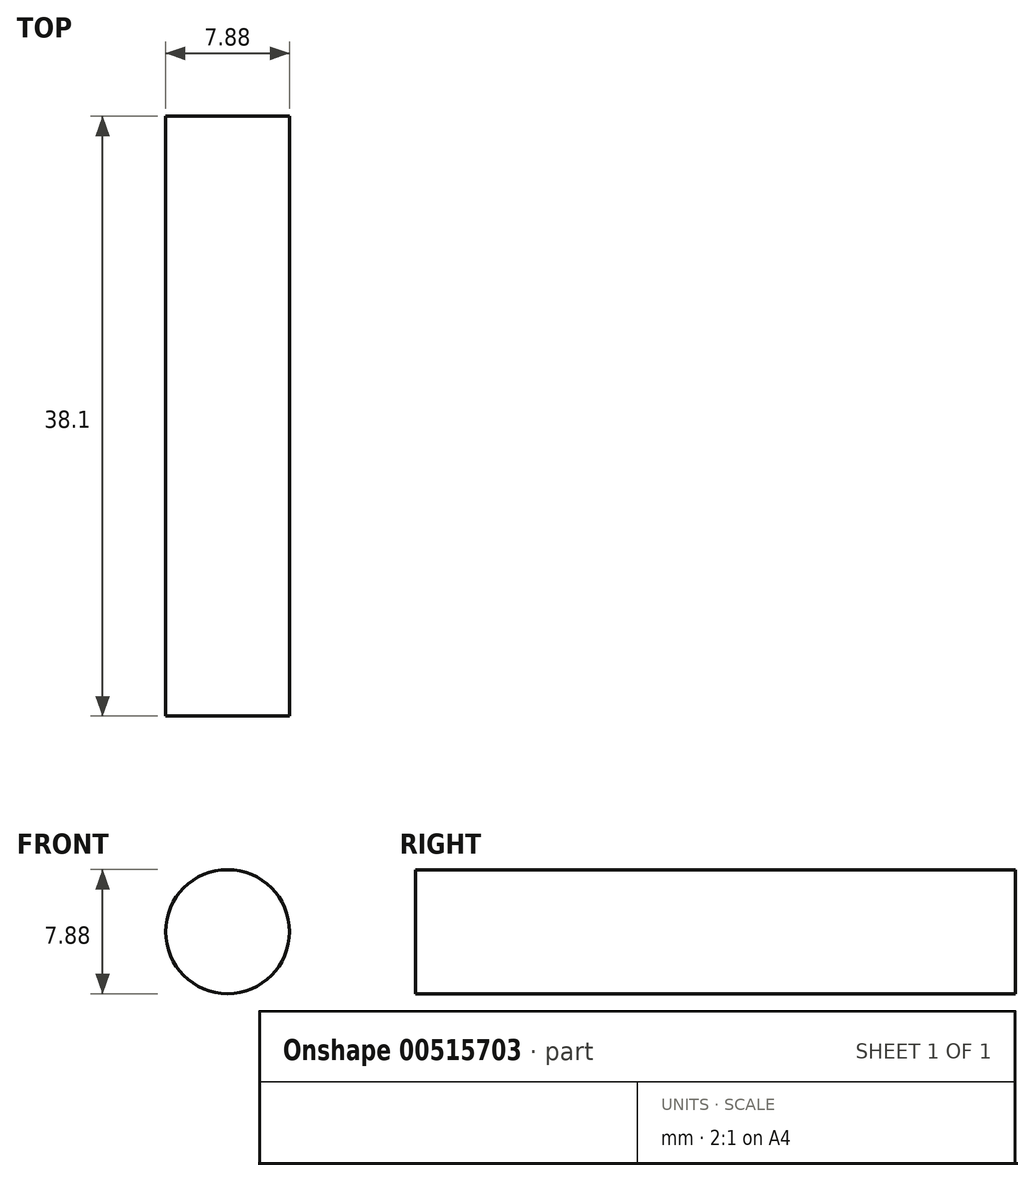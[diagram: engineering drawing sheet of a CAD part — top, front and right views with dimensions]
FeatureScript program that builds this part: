
annotation { "Feature Type Name" : "Feature", "Feature Type Description" : "" }
export const myFeature = defineFeature(function(context is Context, id is Id, definition is map)
    precondition{}
    {
        {
            var Q0;
            Q0=qCreatedBy(makeId("Front.planeOp"),FACE);
            var sketch = newSketch(context, id + "F0", { "sketchPlane" : qUnion([Q0])});
            skCircle(sketch, "E0", {"center": v(0, 0) * mm, "radius": 3.94 * mm});
            skSolve(sketch);
        }
        {
            var Q0;
            Q0=makeQuery(id+"F0.imprint","IMPRINT",FACE,{"disambiguationData":[TD([[makeQuery(id+"F0.imprint","IMPRINT",EDGE,{"derivedFrom":sQuery(id+"F0.wireOp",EDGE,"E0")}),1.0]])]});
            extrude(context, id + "F1", {"entities" : qUnion([Q0]), "endBound" : BoundingType.SYMMETRIC, "depth" : 38.1 * mm, "offsetDistance" : 25.4 * mm});
        }
    });
